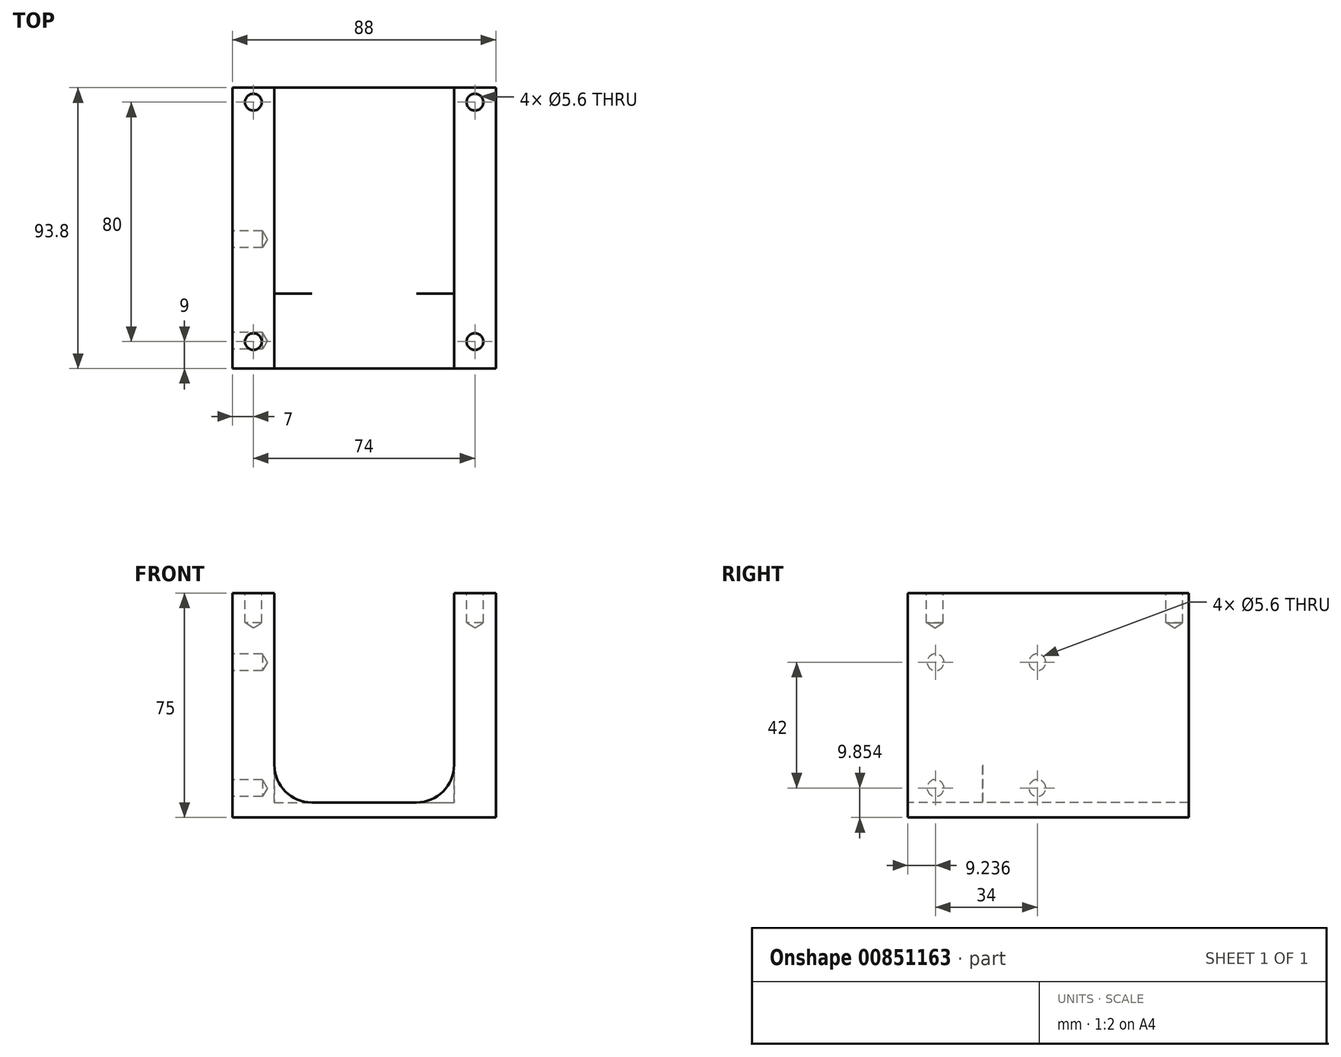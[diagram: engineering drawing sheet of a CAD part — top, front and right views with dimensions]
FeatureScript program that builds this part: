
annotation { "Feature Type Name" : "Feature", "Feature Type Description" : "" }
export const myFeature = defineFeature(function(context is Context, id is Id, definition is map)
    precondition{}
    {
        {
            var Q0;
            Q0=qCreatedBy(makeId("Top.planeOp"),FACE);
            var sketch = newSketch(context, id + "F0", { "sketchPlane" : qUnion([Q0])});
            skLineSegment(sketch, "E0.bottom", {"start": v(37, 40) * mm, "end": v(30, 40) * mm});
            skLineSegment(sketch, "E0.top", {"start": v(37, -40) * mm, "end": v(30, -40) * mm});
            skLineSegment(sketch, "E0.left", {"start": v(37, 40) * mm, "end": v(37, -40) * mm});
            skLineSegment(sketch, "E0.right", {"start": v(-37, 40) * mm, "end": v(-37, -40) * mm});
            skPoint(sketch, "E0.middle", {"position": v(0, 0) * mm});
            skLineSegment(sketch, "E1.left", {"start": v(30, 49) * mm, "end": v(30, -49) * mm});
            skLineSegment(sketch, "E1.right", {"start": v(-30, 49) * mm, "end": v(-30, -49) * mm});
            skLineSegment(sketch, "E2.bottom", {"start": v(44, 49) * mm, "end": v(30, 49) * mm});
            skLineSegment(sketch, "E2.top", {"start": v(44, -49) * mm, "end": v(30, -49) * mm});
            skLineSegment(sketch, "E2.left", {"start": v(44, 49) * mm, "end": v(44, -49) * mm});
            skLineSegment(sketch, "E2.right", {"start": v(-44, 49) * mm, "end": v(-44, -49) * mm});
            skLineSegment(sketch, "E3.trimOffspring", {"start": v(-30, 49) * mm, "end": v(-44, 49) * mm});
            skLineSegment(sketch, "E4.trimOffspring", {"start": v(-30, 40) * mm, "end": v(-37, 40) * mm});
            skLineSegment(sketch, "E5.trimOffspring", {"start": v(-30, -40) * mm, "end": v(-37, -40) * mm});
            skLineSegment(sketch, "E6.trimOffspring", {"start": v(-30, -49) * mm, "end": v(-44, -49) * mm});
            skLineSegment(sketch, "E7.bottom", {"start": v(30, 6.16) * mm, "end": v(-30, 6.16) * mm});
            skLineSegment(sketch, "E7.top", {"start": v(30, -6.16) * mm, "end": v(-30, -6.16) * mm});
            skLineSegment(sketch, "E7.left", {"start": v(30, 6.16) * mm, "end": v(30, -6.16) * mm});
            skLineSegment(sketch, "E7.right", {"start": v(-30, 6.16) * mm, "end": v(-30, -6.16) * mm});
            skSolve(sketch);
        }
        {
            var Q0;
            Q0=makeQuery(id+"F0.imprint","IMPRINT",FACE,{"disambiguationData":[TD([[makeQuery(id+"F0.imprint","IMPRINT",EDGE,{"derivedFrom":sQuery(id+"F0.wireOp",EDGE,"E0.right")}),-1.0]])]});
            var Q1;
            Q1=makeQuery(id+"F0.imprint","IMPRINT",FACE,{"disambiguationData":[TD([[makeQuery(id+"F0.imprint","IMPRINT",EDGE,{"derivedFrom":sQuery(id+"F0.wireOp",EDGE,"E0.right")}),1.0]])]});
            var Q2;
            {var subQ0=sQuery(id+"F0.wireOp",EDGE,"E7.bottom");Q2=makeQuery(id+"F0.imprint","IMPRINT",FACE,{"disambiguationData":[TD([[makeQuery(id+"F0.imprint","IMPRINT",EDGE,{"derivedFrom":subQ0}),1.0]])]});}
            var Q3;
            {var subQ1=sQuery(id+"F0.wireOp",EDGE,"E0.bottom");Q3=makeQuery(id+"F0.imprint","IMPRINT",FACE,{"disambiguationData":[TD([[makeQuery(id+"F0.imprint","IMPRINT",EDGE,{"derivedFrom":subQ1}),1.0]])]});}
            var Q4;
            {var subQ1=sQuery(id+"F0.wireOp",EDGE,"E0.bottom");Q4=makeQuery(id+"F0.imprint","IMPRINT",FACE,{"disambiguationData":[TD([[makeQuery(id+"F0.imprint","IMPRINT",EDGE,{"derivedFrom":subQ1}),-1.0]])]});}
            extrude(context, id + "F1", {"entities" : qUnion([Q0, Q1, Q2, Q3, Q4]), "oppositeDirection" : true, "depth" : 10 * mm, "offsetDistance" : 25 * mm});
        }
        {
            var Q0;
            Q0=makeQuery(id+"F1.opExtrude","CAP_FACE",FACE,{"disambiguationData":[OSD([sQuery(id+"F0.wireOp",EDGE,"E1.left"),sQuery(id+"F0.wireOp",EDGE,"E1.right"),sQuery(id+"F0.wireOp",EDGE,"E2.bottom"),sQuery(id+"F0.wireOp",EDGE,"E2.top"),sQuery(id+"F0.wireOp",EDGE,"E2.left"),sQuery(id+"F0.wireOp",EDGE,"E2.right"),sQuery(id+"F0.wireOp",EDGE,"E3.trimOffspring"),sQuery(id+"F0.wireOp",EDGE,"E6.trimOffspring"),sQuery(id+"F0.wireOp",EDGE,"E7.bottom"),sQuery(id+"F0.wireOp",EDGE,"E7.top")])],"isStart":false});
            extrude(context, id + "F2", {"entities" : qUnion([Q0]), "operationType" : NewBodyOperationType.ADD, "depth" : 60 * mm, "offsetDistance" : 25 * mm});
        }
        {
            var Q0;
            Q0=makeQuery(id+"F2.opExtrude","CAP_FACE",FACE,{"disambiguationData":[OSD([sQuery(id+"F0.wireOp",EDGE,"E1.left"),sQuery(id+"F0.wireOp",EDGE,"E1.right"),sQuery(id+"F0.wireOp",EDGE,"E2.bottom"),sQuery(id+"F0.wireOp",EDGE,"E2.top"),sQuery(id+"F0.wireOp",EDGE,"E2.left"),sQuery(id+"F0.wireOp",EDGE,"E2.right"),sQuery(id+"F0.wireOp",EDGE,"E3.trimOffspring"),sQuery(id+"F0.wireOp",EDGE,"E6.trimOffspring"),sQuery(id+"F0.wireOp",EDGE,"E7.bottom"),sQuery(id+"F0.wireOp",EDGE,"E7.top")])],"isStart":false});
            var sketch = newSketch(context, id + "F3", { "sketchPlane" : qUnion([Q0])});
            skLineSegment(sketch, "E8.bottom", {"start": v(-44, 49) * mm, "end": v(44, 49) * mm});
            skLineSegment(sketch, "E8.top", {"start": v(-44, -49) * mm, "end": v(44, -49) * mm});
            skLineSegment(sketch, "E8.left", {"start": v(-44, 49) * mm, "end": v(-44, -49) * mm});
            skLineSegment(sketch, "E8.right", {"start": v(44, 49) * mm, "end": v(44, -49) * mm});
            skPoint(sketch, "E8.middle", {"position": v(0, 0) * mm});
            skSolve(sketch);
        }
        {
            var Q0;
            Q0 = qSketchRegion(id + "F3", true);
            extrude(context, id + "F4", {"entities" : qUnion([Q0]), "operationType" : NewBodyOperationType.ADD, "depth" : 5 * mm, "offsetDistance" : 25 * mm});
        }
        {
            var Q0;
            {var subQ0=sQuery(id+"F0.wireOp",EDGE,"E7.bottom");Q0=makeQuery(id+"F0.imprint","IMPRINT",FACE,{"disambiguationData":[TD([[makeQuery(id+"F0.imprint","IMPRINT",EDGE,{"derivedFrom":subQ0}),1.0]])]});}
            var Q1;
            {var subQ0=sQuery(id+"F0.wireOp",EDGE,"E2.top");var subQ11=sQuery(id+"F3.wireOp",EDGE,"E8.bottom");Q1=makeQuery(id+"F4.boolean.opBoolean","SPLIT",FACE,{"disambiguationData":[TD([makeQuery(id+"F1.opExtrude","SWEPT_FACE",FACE,{"disambiguationData":[OSD([subQ0])]})])],"derivedFrom":makeQuery(id+"F4.opExtrude","CAP_FACE",FACE,{"disambiguationData":[OSD([subQ11,sQuery(id+"F3.wireOp",EDGE,"E8.top"),sQuery(id+"F3.wireOp",EDGE,"E8.left"),sQuery(id+"F3.wireOp",EDGE,"E8.right")])],"isStart":true})});}
            extrude(context, id + "F5", {"entities" : qUnion([Q0]), "operationType" : NewBodyOperationType.REMOVE, "endBound" : BoundingType.UP_TO_SURFACE, "oppositeDirection" : true, "depth" : 25 * mm, "endBoundEntityFace" : qUnion([Q1]), "offsetDistance" : 25 * mm});
        }
        {
            var Q0;
            Q0=sQuery(id+"F0.wireOp",VERTEX,"E0.right.start");
            var Q1;
            Q1=sQuery(id+"F0.wireOp",VERTEX,"E0.right.end");
            var Q2;
            Q2=sQuery(id+"F0.wireOp",VERTEX,"E0.top.start");
            var Q3;
            Q3=sQuery(id+"F0.wireOp",VERTEX,"E0.bottom.start");
            var Q4;
            Q4=makeQuery(id+"F1.opExtrude","SWEPT_BODY",BODY,{"disambiguationData":[OSD([sQuery(id+"F0.wireOp",EDGE,"E1.left"),sQuery(id+"F0.wireOp",EDGE,"E1.right"),sQuery(id+"F0.wireOp",EDGE,"E2.bottom"),sQuery(id+"F0.wireOp",EDGE,"E2.top"),sQuery(id+"F0.wireOp",EDGE,"E2.left"),sQuery(id+"F0.wireOp",EDGE,"E2.right"),sQuery(id+"F0.wireOp",EDGE,"E3.trimOffspring"),sQuery(id+"F0.wireOp",EDGE,"E6.trimOffspring"),sQuery(id+"F0.wireOp",EDGE,"E7.bottom"),sQuery(id+"F0.wireOp",EDGE,"E7.top")])]});
            hole(context, id + "F6", {"style" : HoleStyle.SIMPLE, "endStyle" : HoleEndStyle.BLIND, "holeDiameter" : 5.6 * mm, "majorDiameter" : 5 * mm, "holeDepth" : 10 * mm, "isTappedThrough" : true, "tappedDepth" : 12 * mm, "tapClearance" : 3, "locations" : qUnion([Q0, Q1, Q2, Q3]), "scope" : qUnion([Q4])});
        }
        {
            var Q0;
            {var subQ0=sQuery(id+"F0.wireOp",EDGE,"E6.trimOffspring");var subQ1=sQuery(id+"F0.wireOp",EDGE,"E2.top");Q0=makeQuery(id+"F4.boolean.opBoolean","MERGE",FACE,{"derivedFrom":[makeQuery(id+"F2.boolean.opBoolean","MERGE",FACE,{"derivedFrom":[makeQuery(id+"F1.opExtrude","SWEPT_FACE",FACE,{"disambiguationData":[OSD([subQ1])]}),makeQuery(id+"F2.opExtrude","SWEPT_FACE",FACE,{"disambiguationData":[OSD([subQ1])]})]}),makeQuery(id+"F2.boolean.opBoolean","MERGE",FACE,{"derivedFrom":[makeQuery(id+"F1.opExtrude","SWEPT_FACE",FACE,{"disambiguationData":[OSD([subQ0])]}),makeQuery(id+"F2.opExtrude","SWEPT_FACE",FACE,{"disambiguationData":[OSD([subQ0])]})]}),makeQuery(id+"F4.opExtrude","SWEPT_FACE",FACE,{"disambiguationData":[OSD([sQuery(id+"F3.wireOp",EDGE,"E8.bottom")])]})]});}
            var sketch = newSketch(context, id + "F7", { "sketchPlane" : qUnion([Q0])});
            skCircle(sketch, "E9", {"center": v(-17.5, -57.5) * mm, "radius": 12.5 * mm});
            skCircle(sketch, "E10", {"center": v(17.5, -57.5) * mm, "radius": 12.5 * mm});
            skSolve(sketch);
        }
        {
            var Q0;
            {var subQ0=sQuery(id+"F7.wireOp",EDGE,"E9");var subQ5=makeQuery(id+"F4.opExtrude","CAP_EDGE",EDGE,{"disambiguationData":[OSD([sQuery(id+"F3.wireOp",EDGE,"E8.bottom")])],"isStart":true});var subQ6=makeQuery(id+"F7.imprint","INTERSECT",VERTEX,{"derivedFrom":[subQ5,subQ0]});Q0=makeQuery(id+"F7.imprint","IMPRINT",FACE,{"disambiguationData":[TD([[makeQuery(id+"F7.imprint","IMPRINT",EDGE,{"disambiguationData":[TD([[subQ6,1.0]])],"derivedFrom":subQ0}),-1.0]])]});}
            var Q1;
            {var subQ0=sQuery(id+"F7.wireOp",EDGE,"E10");var subQ5=makeQuery(id+"F4.opExtrude","CAP_EDGE",EDGE,{"disambiguationData":[OSD([sQuery(id+"F3.wireOp",EDGE,"E8.bottom")])],"isStart":true});var subQ6=makeQuery(id+"F7.imprint","INTERSECT",VERTEX,{"derivedFrom":[subQ5,subQ0]});Q1=makeQuery(id+"F7.imprint","IMPRINT",FACE,{"disambiguationData":[TD([[makeQuery(id+"F7.imprint","IMPRINT",EDGE,{"disambiguationData":[TD([[subQ6,-1.0]])],"derivedFrom":subQ0}),-1.0]])]});}
            extrude(context, id + "F8", {"entities" : qUnion([Q0, Q1]), "operationType" : NewBodyOperationType.ADD, "oppositeDirection" : true, "depth" : 25 * mm, "offsetDistance" : 25 * mm});
        }
        {
            var Q0;
            {var subQ0=sQuery(id+"F0.wireOp",EDGE,"E1.left");var subQ2=sQuery(id+"F0.wireOp",EDGE,"E2.top");var subQ4=sQuery(id+"F0.wireOp",EDGE,"E7.top");var subQ6=sQuery(id+"F0.wireOp",EDGE,"E3.trimOffspring");var subQ8=sQuery(id+"F0.wireOp",EDGE,"E2.bottom");var subQ10=sQuery(id+"F0.wireOp",EDGE,"E7.bottom");var subQ12=sQuery(id+"F0.wireOp",EDGE,"E6.trimOffspring");var subQ13=sQuery(id+"F0.wireOp",EDGE,"E2.left");Q0=makeQuery(id+"F5.boolean.opBoolean","SPLIT",FACE,{"disambiguationData":[TD([makeQuery(id+"F1.opExtrude","SWEPT_FACE",FACE,{"disambiguationData":[OSD([subQ13])]})])],"derivedFrom":makeQuery(id+"F1.opExtrude","CAP_FACE",FACE,{"disambiguationData":[OSD([subQ0,sQuery(id+"F0.wireOp",EDGE,"E1.right"),subQ8,subQ2,subQ13,sQuery(id+"F0.wireOp",EDGE,"E2.right"),subQ6,subQ12,subQ10,subQ4])],"isStart":true})});}
            var sketch = newSketch(context, id + "F9", { "sketchPlane" : qUnion([Q0])});
            skLineSegment(sketch, "E11.bottom", {"start": v(44, 49) * mm, "end": v(-44, 49) * mm});
            skLineSegment(sketch, "E11.top", {"start": v(44, 44.8) * mm, "end": v(-44, 44.8) * mm});
            skLineSegment(sketch, "E11.left", {"start": v(44, 49) * mm, "end": v(44, 44.8) * mm});
            skLineSegment(sketch, "E11.right", {"start": v(-44, 49) * mm, "end": v(-44, 44.8) * mm});
            skSolve(sketch);
        }
        {
            var Q0;
            Q0 = qSketchRegion(id + "F9", true);
            extrude(context, id + "F10", {"entities" : qUnion([Q0]), "operationType" : NewBodyOperationType.REMOVE, "endBound" : BoundingType.THROUGH_ALL, "oppositeDirection" : true, "depth" : 25 * mm, "offsetDistance" : 25 * mm});
        }
        {
            var Q0;
            {var subQ0=sQuery(id+"F0.wireOp",EDGE,"E2.right");Q0=makeQuery(id+"F4.boolean.opBoolean","MERGE",FACE,{"derivedFrom":[makeQuery(id+"F2.boolean.opBoolean","MERGE",FACE,{"derivedFrom":[makeQuery(id+"F1.opExtrude","SWEPT_FACE",FACE,{"disambiguationData":[OSD([subQ0])]}),makeQuery(id+"F2.opExtrude","SWEPT_FACE",FACE,{"disambiguationData":[OSD([subQ0])]})]}),makeQuery(id+"F4.opExtrude","SWEPT_FACE",FACE,{"disambiguationData":[OSD([sQuery(id+"F3.wireOp",EDGE,"E8.left")])]})]});}
            var sketch = newSketch(context, id + "F11", { "sketchPlane" : qUnion([Q0])});
            skLineSegment(sketch, "E12.bottom", {"start": v(39.76, -23.15) * mm, "end": v(5.76, -23.15) * mm});
            skLineSegment(sketch, "E12.top", {"start": v(39.76, -65.15) * mm, "end": v(5.76, -65.15) * mm});
            skLineSegment(sketch, "E12.left", {"start": v(39.76, -23.15) * mm, "end": v(39.76, -65.15) * mm});
            skLineSegment(sketch, "E12.right", {"start": v(5.76, -23.15) * mm, "end": v(5.76, -65.15) * mm});
            skPoint(sketch, "E12.middle", {"position": v(22.76, -44.15) * mm});
            skSolve(sketch);
        }
        {
            var Q0;
            Q0=sQuery(id+"F11.wireOp",VERTEX,"E12.bottom.end");
            var Q1;
            Q1=sQuery(id+"F11.wireOp",VERTEX,"E12.bottom.start");
            var Q2;
            Q2=sQuery(id+"F11.wireOp",VERTEX,"E12.top.end");
            var Q3;
            Q3=sQuery(id+"F11.wireOp",VERTEX,"E12.top.start");
            var Q4;
            Q4=makeQuery(id+"F1.opExtrude","SWEPT_BODY",BODY,{"disambiguationData":[OSD([sQuery(id+"F0.wireOp",EDGE,"E1.left"),sQuery(id+"F0.wireOp",EDGE,"E1.right"),sQuery(id+"F0.wireOp",EDGE,"E2.bottom"),sQuery(id+"F0.wireOp",EDGE,"E2.top"),sQuery(id+"F0.wireOp",EDGE,"E2.left"),sQuery(id+"F0.wireOp",EDGE,"E2.right"),sQuery(id+"F0.wireOp",EDGE,"E3.trimOffspring"),sQuery(id+"F0.wireOp",EDGE,"E6.trimOffspring"),sQuery(id+"F0.wireOp",EDGE,"E7.bottom"),sQuery(id+"F0.wireOp",EDGE,"E7.top")])]});
            hole(context, id + "F12", {"style" : HoleStyle.SIMPLE, "endStyle" : HoleEndStyle.BLIND, "holeDiameter" : 5.6 * mm, "majorDiameter" : 5 * mm, "holeDepth" : 10 * mm, "isTappedThrough" : true, "tappedDepth" : 12 * mm, "tapClearance" : 3, "locations" : qUnion([Q0, Q1, Q2, Q3]), "scope" : qUnion([Q4])});
        }
    });
